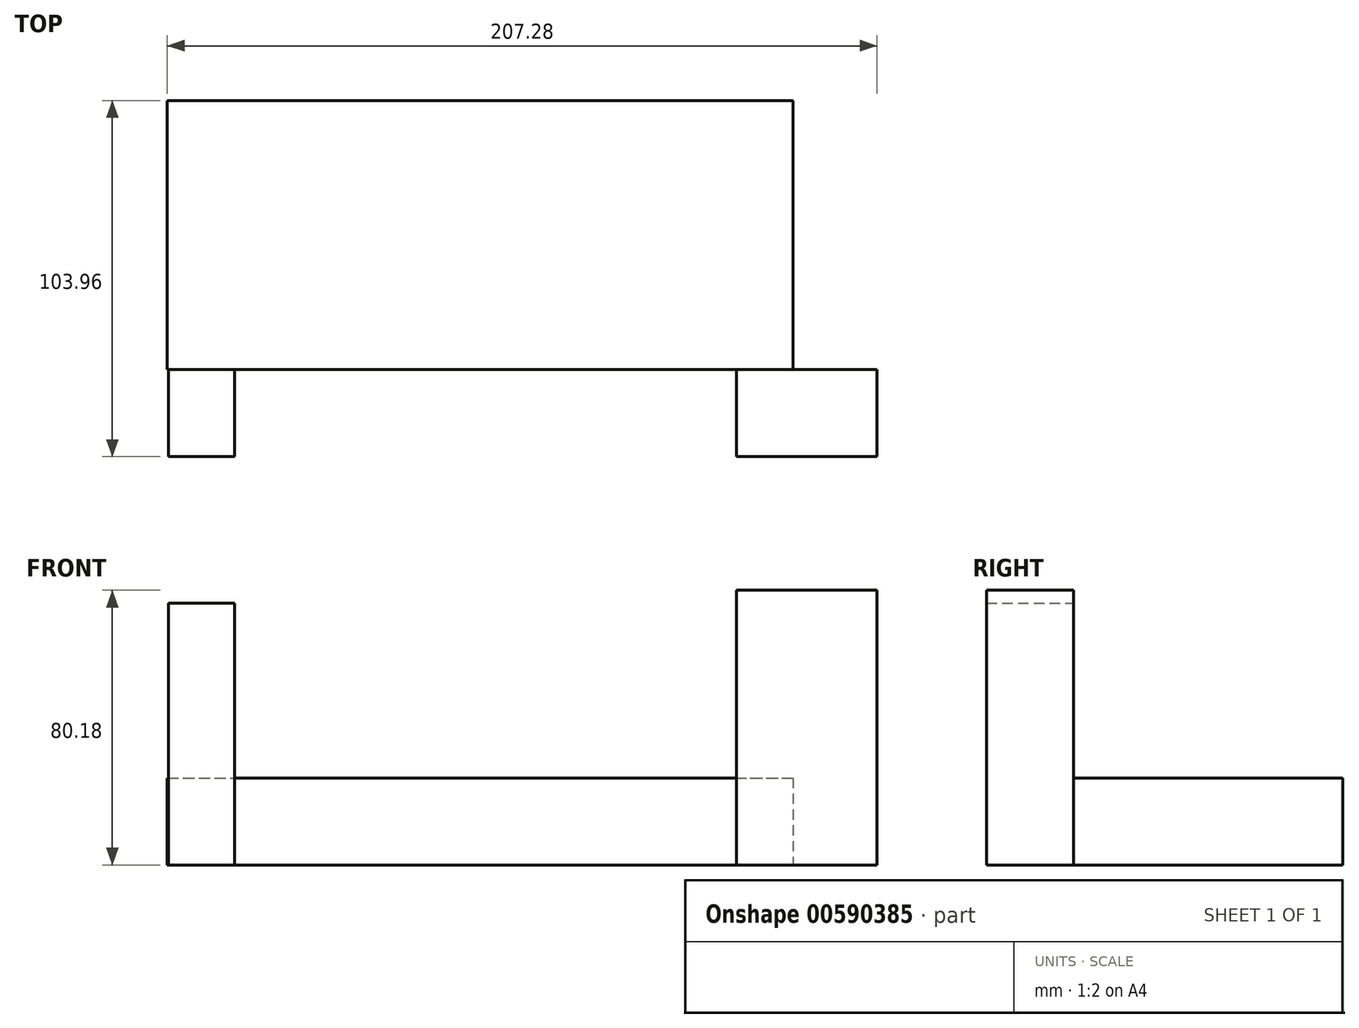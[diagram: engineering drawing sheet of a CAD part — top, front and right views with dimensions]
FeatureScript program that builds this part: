
annotation { "Feature Type Name" : "Feature", "Feature Type Description" : "" }
export const myFeature = defineFeature(function(context is Context, id is Id, definition is map)
    precondition{}
    {
        {
            var Q0;
            Q0=qCreatedBy(makeId("Top.planeOp"),FACE);
            var sketch = newSketch(context, id + "F0", { "sketchPlane" : qUnion([Q0])});
            skLineSegment(sketch, "E0.bottom", {"start": v(-147.3, 78.56) * mm, "end": v(35.42, 78.56) * mm});
            skLineSegment(sketch, "E0.top", {"start": v(-147.3, 0) * mm, "end": v(35.42, 0) * mm});
            skLineSegment(sketch, "E0.left", {"start": v(-147.3, 78.56) * mm, "end": v(-147.3, 0) * mm});
            skLineSegment(sketch, "E0.right", {"start": v(35.42, 78.56) * mm, "end": v(35.42, 0) * mm});
            skSolve(sketch);
        }
        {
            var Q0;
            Q0=makeQuery(id+"F0.imprint","IMPRINT",FACE,{"disambiguationData":[TD([[makeQuery(id+"F0.imprint","IMPRINT",EDGE,{"derivedFrom":sQuery(id+"F0.wireOp",EDGE,"E0.bottom")}),-1.0]])]});
            extrude(context, id + "F1", {"entities" : qUnion([Q0]), "depth" : 25.4 * mm, "offsetDistance" : 25.4 * mm});
        }
        {
            var Q0;
            Q0=qCreatedBy(makeId("Front.planeOp"),FACE);
            var sketch = newSketch(context, id + "F2", { "sketchPlane" : qUnion([Q0])});
            skLineSegment(sketch, "E1.bottom", {"start": v(34.81, 3) * mm, "end": v(25.46, 3) * mm});
            skLineSegment(sketch, "E1.top", {"start": v(34.81, 76.46) * mm, "end": v(25.46, 76.46) * mm});
            skLineSegment(sketch, "E1.left", {"start": v(34.81, 3) * mm, "end": v(34.81, 76.46) * mm});
            skLineSegment(sketch, "E1.right", {"start": v(25.46, 3) * mm, "end": v(25.46, 76.46) * mm});
            skLineSegment(sketch, "E2.bottom", {"start": v(-146.98, 0) * mm, "end": v(-127.7, 0) * mm});
            skLineSegment(sketch, "E2.top", {"start": v(-146.98, 76.46) * mm, "end": v(-127.7, 76.46) * mm});
            skLineSegment(sketch, "E2.left", {"start": v(-146.98, 0) * mm, "end": v(-146.98, 76.46) * mm});
            skLineSegment(sketch, "E2.right", {"start": v(-127.7, 0) * mm, "end": v(-127.7, 76.46) * mm});
            skSolve(sketch);
        }
        {
            var Q0;
            Q0=makeQuery(id+"F2.imprint","IMPRINT",FACE,{"disambiguationData":[TD([[makeQuery(id+"F2.imprint","IMPRINT",EDGE,{"derivedFrom":sQuery(id+"F2.wireOp",EDGE,"E2.bottom")}),1.0]])]});
            extrude(context, id + "F3", {"entities" : qUnion([Q0]), "operationType" : NewBodyOperationType.ADD, "depth" : 25.4 * mm, "offsetDistance" : 25.4 * mm});
        }
        {
            var Q0;
            Q0=qCreatedBy(makeId("Front.planeOp"),FACE);
            var sketch = newSketch(context, id + "F4", { "sketchPlane" : qUnion([Q0])});
            skLineSegment(sketch, "E3.bottom", {"start": v(34.57, 0) * mm, "end": v(18.88, 0) * mm});
            skLineSegment(sketch, "E3.top", {"start": v(34.57, 80.18) * mm, "end": v(18.88, 80.18) * mm});
            skLineSegment(sketch, "E3.left", {"start": v(34.57, 0) * mm, "end": v(34.57, 80.18) * mm});
            skLineSegment(sketch, "E3.right", {"start": v(18.88, 0) * mm, "end": v(18.88, 80.18) * mm});
            skSolve(sketch);
        }
        {
            var Q0;
            Q0=makeQuery(id+"F4.imprint","IMPRINT",FACE,{"disambiguationData":[TD([[makeQuery(id+"F4.imprint","IMPRINT",EDGE,{"derivedFrom":sQuery(id+"F4.wireOp",EDGE,"E3.bottom")}),-1.0]])]});
            extrude(context, id + "F5", {"entities" : qUnion([Q0]), "operationType" : NewBodyOperationType.ADD, "depth" : 25.4 * mm, "offsetDistance" : 25.4 * mm});
        }
        {
            var Q0;
            Q0=makeQuery(id+"F5.opExtrude","SWEPT_FACE",FACE,{"disambiguationData":[OSD([sQuery(id+"F4.wireOp",EDGE,"E3.left")])]});
            extrude(context, id + "F6", {"entities" : qUnion([Q0]), "operationType" : NewBodyOperationType.ADD, "depth" : 25.4 * mm, "offsetDistance" : 25.4 * mm});
        }
    });
